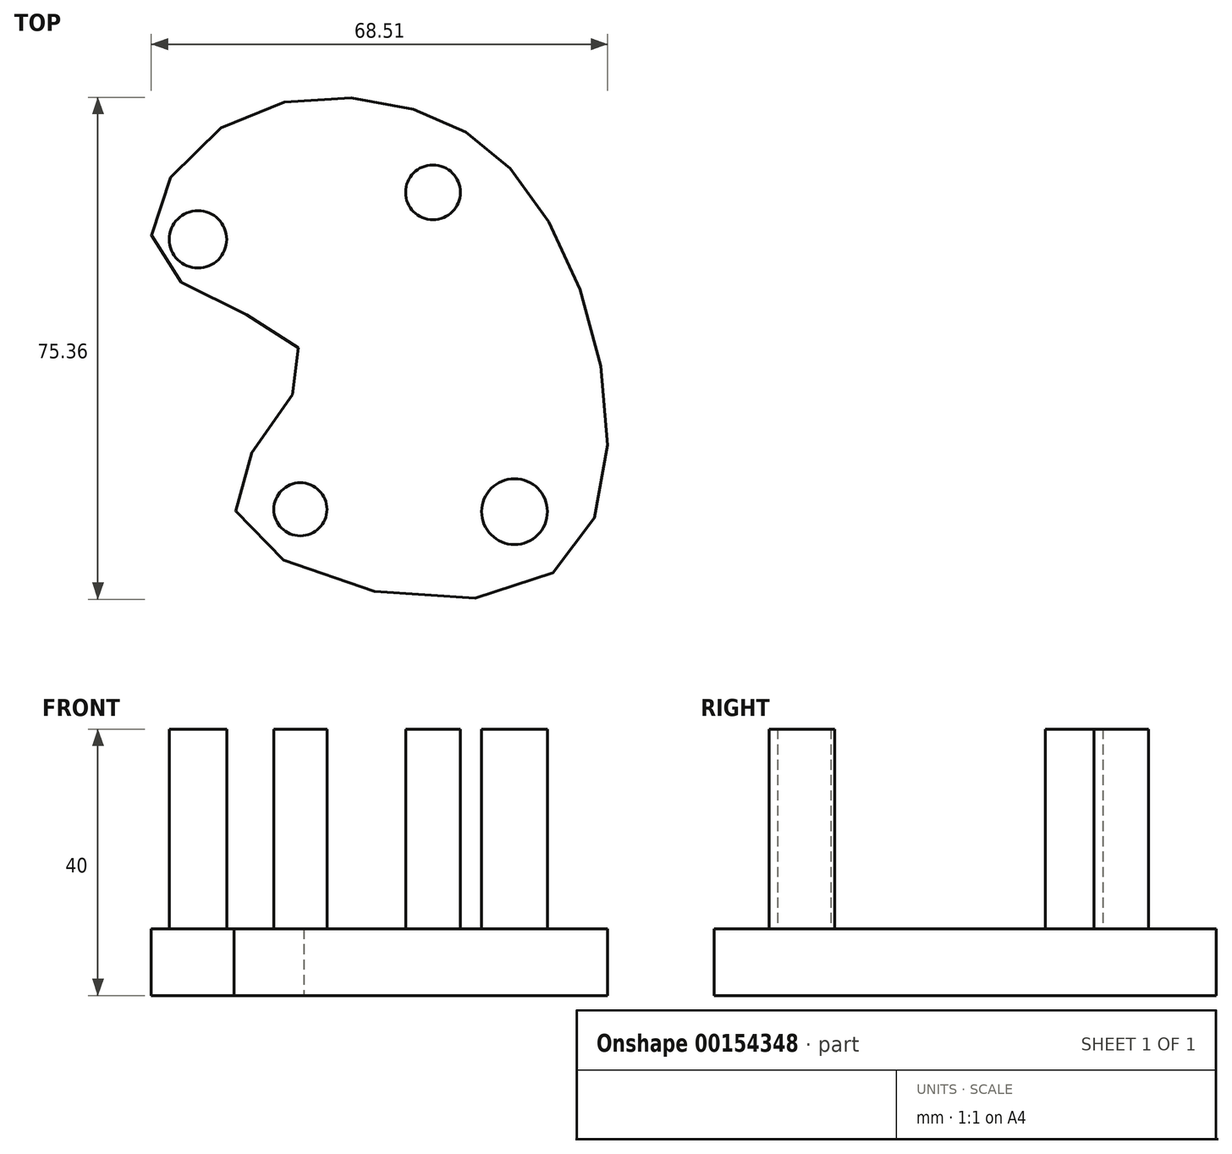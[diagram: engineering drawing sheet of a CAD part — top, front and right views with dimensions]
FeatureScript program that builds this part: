
annotation { "Feature Type Name" : "Feature", "Feature Type Description" : "" }
export const myFeature = defineFeature(function(context is Context, id is Id, definition is map)
    precondition{}
    {
        {
            var Q0;
            Q0=qCreatedBy(makeId("Top.planeOp"),FACE);
            var sketch = newSketch(context, id + "F0", { "sketchPlane" : qUnion([Q0])});
            skFitSpline(sketch, "E0", {"points": [v(-39.64, 45.07) * mm, v(-12.33, 48.3) * mm, v(5.58, 36.85) * mm, v(18.2, 3.08) * mm, v(5.29, -24.22) * mm, v(-37.58, -11.9) * mm, v(-27.3, 10.42) * mm, v(-48.74, 24.81) * mm, v(-39.64, 45.07) * mm]});
            skSolve(sketch);
        }
        {
            var Q0;
            Q0=makeQuery(id+"F0.imprint","IMPRINT",FACE,{"disambiguationData":[TD([[makeQuery(id+"F0.imprint","IMPRINT",EDGE,{"derivedFrom":sQuery(id+"F0.wireOp",EDGE,"E0")}),-1.0]])]});
            extrude(context, id + "F1", {"entities" : qUnion([Q0]), "depth" : 10 * mm});
        }
        {
            var Q0;
            Q0=qCreatedBy(makeId("Top.planeOp"),FACE);
            var sketch = newSketch(context, id + "F2", { "sketchPlane" : qUnion([Q0])});
            skCircle(sketch, "E1", {"center": v(-27.73, -12.2) * mm, "radius": 3.98 * mm});
            skCircle(sketch, "E2", {"center": v(4.42, -12.56) * mm, "radius": 4.94 * mm});
            skCircle(sketch, "E3", {"center": v(-43.1, 28.33) * mm, "radius": 4.3 * mm});
            skCircle(sketch, "E4", {"center": v(-7.83, 35.39) * mm, "radius": 4.11 * mm});
            skSolve(sketch);
        }
        {
            var Q0;
            Q0=makeQuery(id+"F2.imprint","IMPRINT",FACE,{"disambiguationData":[TD([[makeQuery(id+"F2.imprint","IMPRINT",EDGE,{"derivedFrom":sQuery(id+"F2.wireOp",EDGE,"E2")}),1.0]])]});
            var Q1;
            Q1=makeQuery(id+"F2.imprint","IMPRINT",FACE,{"disambiguationData":[TD([[makeQuery(id+"F2.imprint","IMPRINT",EDGE,{"derivedFrom":sQuery(id+"F2.wireOp",EDGE,"E4")}),1.0]])]});
            var Q2;
            Q2=makeQuery(id+"F2.imprint","IMPRINT",FACE,{"disambiguationData":[TD([[makeQuery(id+"F2.imprint","IMPRINT",EDGE,{"derivedFrom":sQuery(id+"F2.wireOp",EDGE,"E3")}),1.0]])]});
            var Q3;
            Q3=makeQuery(id+"F2.imprint","IMPRINT",FACE,{"disambiguationData":[TD([[makeQuery(id+"F2.imprint","IMPRINT",EDGE,{"derivedFrom":sQuery(id+"F2.wireOp",EDGE,"E1")}),1.0]])]});
            extrude(context, id + "F3", {"entities" : qUnion([Q0, Q1, Q2, Q3]), "operationType" : NewBodyOperationType.ADD, "depth" : 40 * mm});
        }
    });
